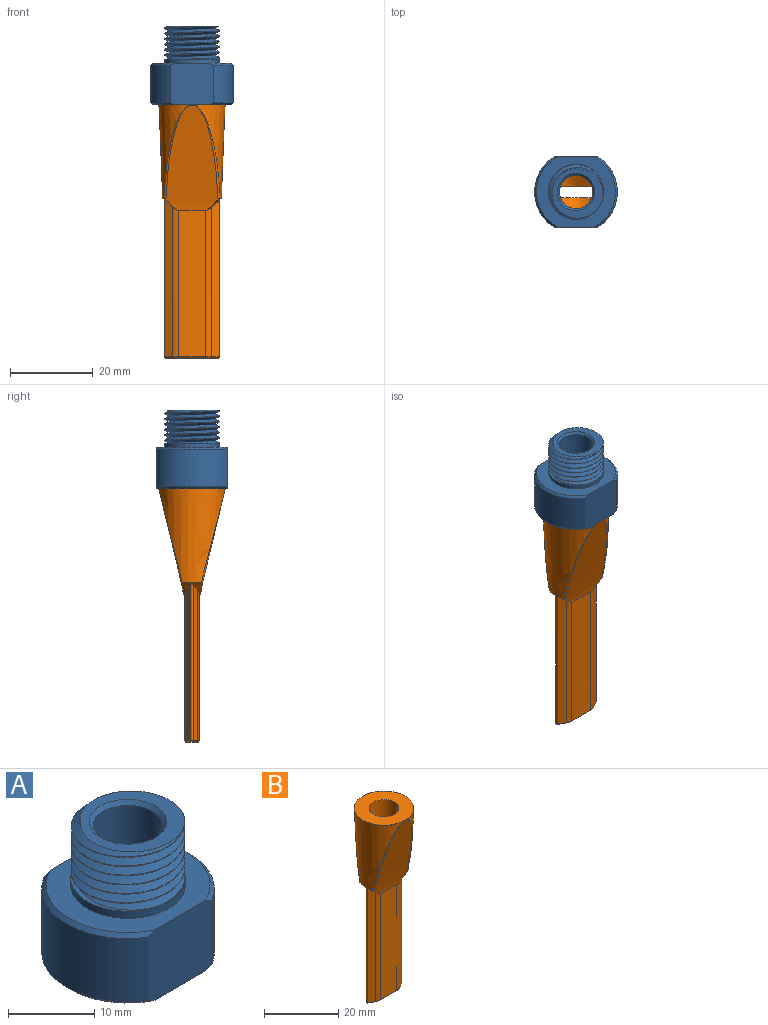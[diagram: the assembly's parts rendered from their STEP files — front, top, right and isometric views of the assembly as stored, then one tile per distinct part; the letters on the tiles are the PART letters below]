
ASSEMBLY  parts=2 mates=1
PART A: 21 faces, bbox 20x17.9x19.8 mm
  f0: plane 0.34x0.29mm, normal (0,1,0), area 0mm2, adj f11,f12,f13
  f1: cylinder r=6.58mm len=13.17mm, axis (0,0,1), area 25.1mm2, adj f6,f10,f11,f12,f14
  f2: cylinder r=10mm len=17mm, axis (0,0,1), area 182.9mm2, adj f7,f8,f17,f19
  f3: cylinder r=10mm len=17mm, axis (0,0,1), area 182.9mm2, adj f7,f8,f16,f18
  f4: plane 19x17mm, normal (0,0,1), area 133.2mm2, adj f7,f8,f15,f18,f19
  f5: plane 19x17mm, normal (0,0,-1), area 221.8mm2, adj f7,f8,f9,f16,f17
  f6: plane 12.25x12.24mm, normal (0,0,1), area 53.8mm2, adj f1,f11,f12,f20
  f7: plane 10.57x10.04mm, normal (0,-1,0), area 104.4mm2, adj f2,f3,f4,f5,f16,f17,f18,f19
  f8: plane 10.57x10.04mm, normal (0,1,0), area 104.4mm2, adj f2,f3,f4,f5,f16,f17,f18,f19
  f9: cylinder r=4mm len=18.5mm, axis (0,0,1), area 465mm2, adj f5,f20
  f10: plane 0.48x0.28mm, normal (0,1,0), area 0.1mm2, adj f1,f12,f14
  f11: bspline ~15.21x13.17mm, area 285.1mm2, adj f0,f1,f6,f12,f13,f14
  f12: bspline ~15.21x13.17mm, area 281.4mm2, adj f0,f1,f6,f10,f11,f13,f14
  f13: cylinder r=5.84mm len=10.05mm, axis (0,0,-1), area 3.1mm2, adj f0,f11,f12,f14
  f14: plane 13.33x13.33mm, normal (0,0,1), area 18mm2, adj f1,f10,f11,f12,f13,f15
  f15: cylinder r=6.65mm len=13.3mm, axis (0,0,-1), area 41.8mm2, adj f4,f14
  f16: cone r=10mm half-angle=45deg, axis (0,0,1), area 14.6mm2, adj f3,f5,f7,f8
  f17: cone r=10mm half-angle=45deg, axis (0,0,1), area 14.6mm2, adj f2,f5,f7,f8
  f18: cone r=9.5mm half-angle=45deg, axis (0,0,-1), area 14.6mm2, adj f3,f4,f7,f8
  f19: cone r=9.5mm half-angle=45deg, axis (0,0,-1), area 14.6mm2, adj f2,f4,f7,f8
  f20: cone r=4mm half-angle=45deg, axis (0,0,1), area 18.9mm2, adj f6,f9
PART B: 41 faces, bbox 22.1x22.1x67.1 mm
  f0: cone r=8mm half-angle=2.2deg, axis (0,0,1), area 320.3mm2, adj f7,f8,f39,f40
  f1: plane 59.07x13.57mm, normal (0,-1,0), area 390.5mm2, adj f3,f16,f18,f19,f21,f28
  f2: plane 59.07x13.57mm, normal (0,1,0), area 390.5mm2, adj f3,f16,f17,f20,f21,f26
  f3: plane 2.8x2mm, normal (0,0,-1), area 2.3mm2, adj f1,f2,f19,f20,f27
  f4: plane 7.22x0.33mm, normal (0,0,-1), area 2.1mm2, adj f6,f7,f13,f25,f33,f34
  f5: cone r=8mm half-angle=2.2deg, axis (0,0,1), area 320.3mm2, adj f6,f8,f39,f40
  f6: cone r=7.12mm half-angle=46.1deg, axis (0,0,1), area 13.2mm2, adj f4,f5,f9,f14,f15,f24,f25,f34
  f7: cone r=7.12mm half-angle=46.1deg, axis (0,0,1), area 13.2mm2, adj f0,f4,f9,f11,f12,f24,f25,f33
  f8: plane 16.1x16.1mm, normal (0,0,1), area 150.8mm2, adj f0,f5,f27,f39,f40
  f9: plane 7.22x0.33mm, normal (0,0,-1), area 2.1mm2, adj f6,f7,f10,f24,f35,f36
  f10: plane 35.2x6.38mm, normal (0,1,0), area 224.5mm2, adj f9,f23,f35,f36
  f11: plane 37.9x2.09mm, normal (0.5,0.86,0), area 79.1mm2, adj f7,f30,f36,f38
  f12: plane 37.9x2.09mm, normal (0.5,-0.86,0), area 79.1mm2, adj f7,f29,f33,f38
  f13: plane 35.2x6.38mm, normal (0,-1,0), area 224.5mm2, adj f4,f22,f33,f34
  f14: plane 37.9x2.09mm, normal (-0.5,-0.86,0), area 79.1mm2, adj f6,f31,f34,f37
  f15: plane 37.9x2.09mm, normal (-0.5,0.86,0), area 79.1mm2, adj f6,f32,f35,f37
  f16: plane 12.81x2.9mm, normal (0,0,-1), area 3.3mm2, adj f1,f2,f17,f18,f19,f20,f22,f23
  f17: plane 53x2mm, normal (0.57,0.82,0), area 129.4mm2, adj f2,f16,f18,f21
  f18: plane 53x2mm, normal (0.57,-0.82,0), area 129.4mm2, adj f1,f16,f17,f21
  f19: plane 53x2mm, normal (-0.57,-0.82,0), area 129.4mm2, adj f1,f3,f16,f20
  f20: plane 53x2mm, normal (-0.57,0.82,0), area 129.4mm2, adj f2,f3,f16,f19
  f21: plane 2.8x2mm, normal (0,0,-1), area 2.3mm2, adj f1,f2,f17,f18,f27
  f22: plane 8x0.35mm, normal (0,-0.71,-0.71), area 3.3mm2, adj f13,f16,f29,f31,f33,f34
  f23: plane 8x0.35mm, normal (0,0.71,-0.71), area 3.3mm2, adj f10,f16,f30,f32,f35,f36
  f24: extruded ~25.48x12.85mm, area 255.4mm2, adj f6,f7,f9,f40
  f25: extruded ~25.46x12.57mm, area 251mm2, adj f4,f6,f7,f39
  f26: cone r=0mm half-angle=59deg, axis (0,0,1), area 0mm2, adj f2,f27
  f27: cylinder r=4mm len=8mm, axis (0,0,1), area 201.1mm2, adj f3,f8,f21,f26,f28
  f28: cone r=0mm half-angle=59deg, axis (0,0,1), area 0mm2, adj f1,f27
  f29: plane 2.85x1.72mm, normal (0.36,-0.61,-0.71), area 1.3mm2, adj f12,f16,f22,f30,f33,f38
  f30: plane 2.85x1.72mm, normal (0.36,0.61,-0.71), area 1.3mm2, adj f11,f16,f23,f29,f36,f38
  f31: plane 2.85x1.72mm, normal (-0.36,-0.61,-0.71), area 1.3mm2, adj f14,f16,f22,f32,f34,f37
  f32: plane 2.85x1.72mm, normal (-0.36,0.61,-0.71), area 1.3mm2, adj f15,f16,f23,f31,f35,f37
  f33: cylinder r=3mm len=36.16mm, axis (0,0,-1), area 56.3mm2, adj f4,f7,f12,f13,f22,f29
  f34: cylinder r=3mm len=36.16mm, axis (0,0,1), area 56.3mm2, adj f4,f6,f13,f14,f22,f31
  f35: cylinder r=3mm len=36.16mm, axis (0,0,-1), area 56.3mm2, adj f6,f9,f10,f15,f23,f32
  f36: cylinder r=3mm len=36.16mm, axis (0,0,1), area 56.3mm2, adj f7,f9,f10,f11,f23,f30
  f37: cylinder r=0.3mm len=37.81mm, axis (0,0,1), area 23.6mm2, adj f6,f14,f15,f31,f32
  f38: cylinder r=0.3mm len=37.81mm, axis (0,0,1), area 23.6mm2, adj f7,f11,f12,f29,f30
  f39: bspline ~23.67x13.57mm, area 19.7mm2, adj f0,f5,f6,f7,f8,f25
  f40: bspline ~23.56x13.46mm, area 11.6mm2, adj f0,f5,f6,f7,f8,f24
PLACE A t=(-18.75,-1.25,-47.18)mm
PLACE B t=(-18.75,-1.25,-21.2)mm
MATE fastened A.f1 <-> B.f0  axis (0,0,1) through (-18.75,-1.25,-5.59)mm
